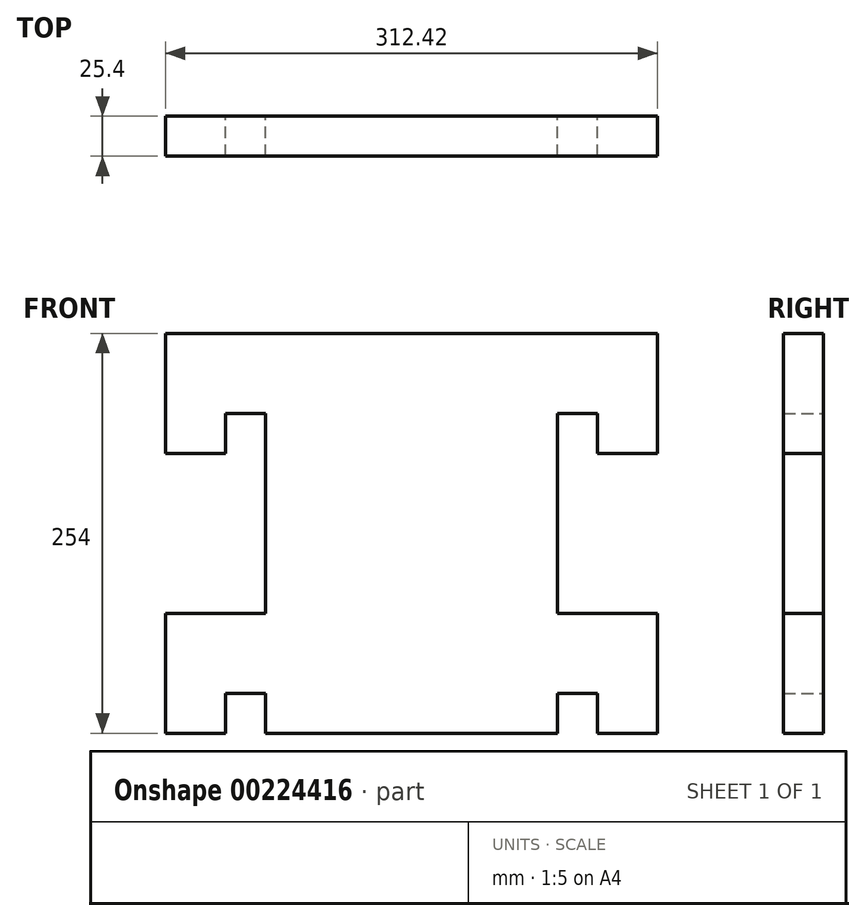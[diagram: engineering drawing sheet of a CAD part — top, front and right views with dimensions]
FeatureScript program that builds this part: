
annotation { "Feature Type Name" : "Feature", "Feature Type Description" : "" }
export const myFeature = defineFeature(function(context is Context, id is Id, definition is map)
    precondition{}
    {
        {
            var Q0;
            Q0=qCreatedBy(makeId("Front.planeOp"),FACE);
            var sketch = newSketch(context, id + "F0", { "sketchPlane" : qUnion([Q0])});
            skLineSegment(sketch, "E0.bottom", {"start": v(92.71, 127) * mm, "end": v(-92.7, 127) * mm});
            skLineSegment(sketch, "E0.top", {"start": v(92.7, -127) * mm, "end": v(-92.71, -127) * mm});
            skLineSegment(sketch, "E0.left", {"start": v(92.7, 76.2) * mm, "end": v(92.7, -50.8) * mm});
            skLineSegment(sketch, "E0.right", {"start": v(-92.7, 76.2) * mm, "end": v(-92.71, -50.8) * mm});
            skPoint(sketch, "E0.middle", {"position": v(0, 0) * mm});
            skLineSegment(sketch, "E1", {"start": v(92.71, 127) * mm, "end": v(156.2, 127) * mm});
            skLineSegment(sketch, "E2", {"start": v(156.2, 127) * mm, "end": v(156.2, 50.8) * mm});
            skLineSegment(sketch, "E3", {"start": v(156.2, 50.8) * mm, "end": v(118.11, 50.8) * mm});
            skLineSegment(sketch, "E4", {"start": v(118.11, 50.8) * mm, "end": v(118.1, 76.2) * mm});
            skLineSegment(sketch, "E5", {"start": v(118.11, 76.2) * mm, "end": v(92.7, 76.2) * mm});
            skLineSegment(sketch, "E6", {"start": v(92.7, -127) * mm, "end": v(92.7, -101.6) * mm});
            skLineSegment(sketch, "E7", {"start": v(92.7, -50.8) * mm, "end": v(156.2, -50.8) * mm});
            skLineSegment(sketch, "E8", {"start": v(156.2, -50.8) * mm, "end": v(156.2, -127) * mm});
            skLineSegment(sketch, "E9", {"start": v(156.2, -127) * mm, "end": v(118.1, -127) * mm});
            skLineSegment(sketch, "E10", {"start": v(118.1, -127) * mm, "end": v(118.1, -101.6) * mm});
            skLineSegment(sketch, "E11", {"start": v(118.1, -101.6) * mm, "end": v(92.7, -101.6) * mm});
            skLineSegment(sketch, "E12.MirrorCS", {"start": v(-118.11, 50.8) * mm, "end": v(-118.1, 76.2) * mm});
            skLineSegment(sketch, "E13.MirrorCS", {"start": v(-156.2, 50.8) * mm, "end": v(-118.11, 50.8) * mm});
            skLineSegment(sketch, "E14.MirrorCS", {"start": v(-118.11, 76.2) * mm, "end": v(-92.7, 76.2) * mm});
            skLineSegment(sketch, "E15.MirrorCS", {"start": v(-92.71, 127) * mm, "end": v(-156.2, 127) * mm});
            skLineSegment(sketch, "E16.MirrorCS", {"start": v(-156.2, 127) * mm, "end": v(-156.2, 50.8) * mm});
            skLineSegment(sketch, "E17.MirrorCS", {"start": v(-156.2, -127) * mm, "end": v(-118.1, -127) * mm});
            skLineSegment(sketch, "E18.MirrorCS", {"start": v(-156.2, -50.8) * mm, "end": v(-156.2, -127) * mm});
            skLineSegment(sketch, "E19.MirrorCS", {"start": v(-92.7, -50.8) * mm, "end": v(-156.2, -50.8) * mm});
            skLineSegment(sketch, "E20.MirrorCS", {"start": v(-92.7, -127) * mm, "end": v(-92.7, -101.6) * mm});
            skLineSegment(sketch, "E21.MirrorCS", {"start": v(-118.1, -101.6) * mm, "end": v(-92.7, -101.6) * mm});
            skLineSegment(sketch, "E22.MirrorCS", {"start": v(-118.1, -127) * mm, "end": v(-118.1, -101.6) * mm});
            skLineSegment(sketch, "E23.trimOffspring", {"start": v(-92.71, -101.6) * mm, "end": v(-92.71, -127) * mm});
            skLineSegment(sketch, "E24.trimOffspring", {"start": v(92.7, -101.6) * mm, "end": v(92.7, -127) * mm});
            skSolve(sketch);
        }
        {
            var Q0;
            Q0 = qSketchRegion(id + "F0", true);
            extrude(context, id + "F1", {"entities" : qUnion([Q0]), "depth" : 25.4 * mm});
        }
    });
